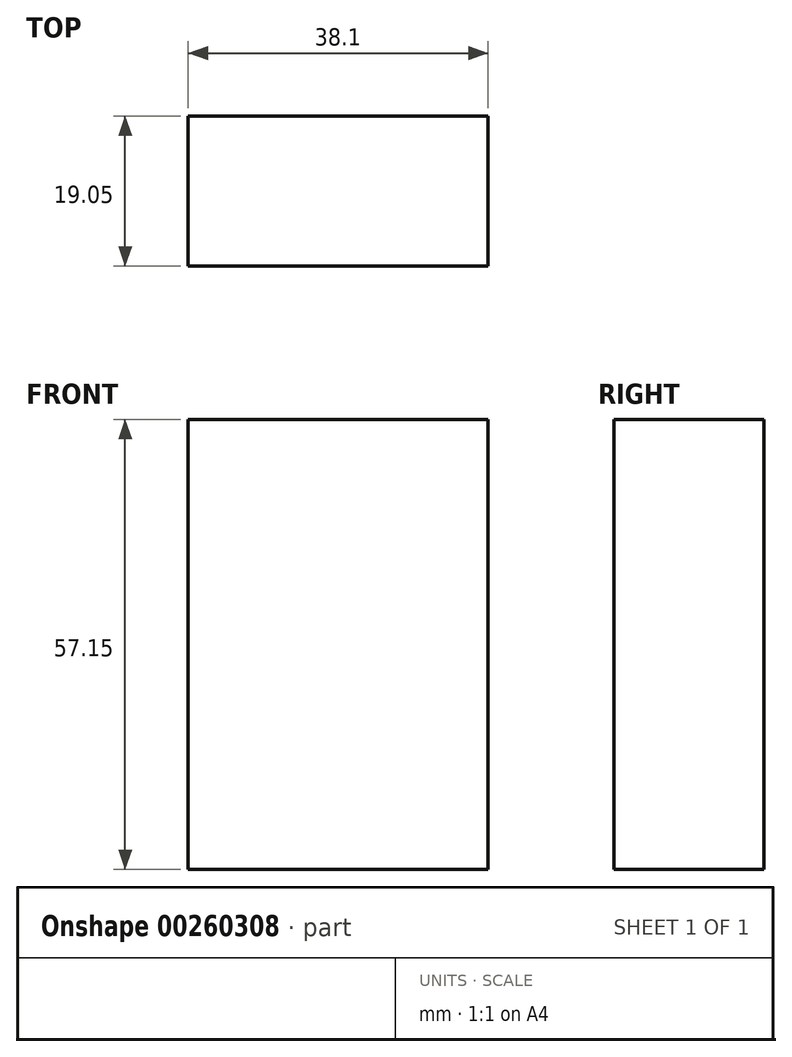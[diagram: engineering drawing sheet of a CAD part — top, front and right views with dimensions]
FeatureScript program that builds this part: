
annotation { "Feature Type Name" : "Feature", "Feature Type Description" : "" }
export const myFeature = defineFeature(function(context is Context, id is Id, definition is map)
    precondition{}
    {
        {
            var Q0;
            Q0=qCreatedBy(makeId("Front.planeOp"),FACE);
            var sketch = newSketch(context, id + "F0", { "sketchPlane" : qUnion([Q0])});
            skLineSegment(sketch, "E0.bottom", {"start": v(-54.15, 47.37) * mm, "end": v(-35.1, 47.37) * mm});
            skLineSegment(sketch, "E0.top", {"start": v(-54.15, 28.32) * mm, "end": v(-35.1, 28.32) * mm});
            skLineSegment(sketch, "E0.left", {"start": v(-54.15, 47.37) * mm, "end": v(-54.15, 28.32) * mm});
            skLineSegment(sketch, "E0.right", {"start": v(-35.1, 47.37) * mm, "end": v(-35.1, 28.32) * mm});
            skLineSegment(sketch, "E1.MirrorCS", {"start": v(-54.15, 9.27) * mm, "end": v(-54.15, 28.32) * mm});
            skLineSegment(sketch, "E2.MirrorCS", {"start": v(-35.1, 9.27) * mm, "end": v(-35.1, 28.32) * mm});
            skLineSegment(sketch, "E3.MirrorCS", {"start": v(-54.15, 9.27) * mm, "end": v(-35.1, 9.27) * mm});
            skLineSegment(sketch, "E4.MirrorCS", {"start": v(-54.15, 9.27) * mm, "end": v(-54.15, -9.78) * mm});
            skLineSegment(sketch, "E5.MirrorCS", {"start": v(-35.1, 9.27) * mm, "end": v(-35.1, -9.78) * mm});
            skLineSegment(sketch, "E6.MirrorCS", {"start": v(-54.15, -9.78) * mm, "end": v(-35.1, -9.78) * mm});
            skLineSegment(sketch, "E7.MirrorCS", {"start": v(-16.05, 47.37) * mm, "end": v(-35.1, 47.37) * mm});
            skLineSegment(sketch, "E8.MirrorCS", {"start": v(-16.05, 47.37) * mm, "end": v(-16.05, 28.32) * mm});
            skLineSegment(sketch, "E9.MirrorCS", {"start": v(-16.05, 28.32) * mm, "end": v(-35.1, 28.32) * mm});
            skLineSegment(sketch, "E10.MirrorCS", {"start": v(-16.05, 9.27) * mm, "end": v(-16.05, 28.32) * mm});
            skLineSegment(sketch, "E11.MirrorCS", {"start": v(-16.05, 9.27) * mm, "end": v(-35.1, 9.27) * mm});
            skLineSegment(sketch, "E12.MirrorCS", {"start": v(-16.05, 9.27) * mm, "end": v(-16.05, -9.78) * mm});
            skLineSegment(sketch, "E13.MirrorCS", {"start": v(-16.05, -9.78) * mm, "end": v(-35.1, -9.78) * mm});
            skSolve(sketch);
        }
        {
            var Q0;
            Q0=makeQuery(id+"F0.imprint","IMPRINT",FACE,{"disambiguationData":[TD([[makeQuery(id+"F0.imprint","IMPRINT",EDGE,{"derivedFrom":sQuery(id+"F0.wireOp",EDGE,"E3.MirrorCS")}),-1.0]])]});
            var Q1;
            Q1=makeQuery(id+"F0.imprint","IMPRINT",FACE,{"disambiguationData":[TD([[makeQuery(id+"F0.imprint","IMPRINT",EDGE,{"derivedFrom":sQuery(id+"F0.wireOp",EDGE,"E5.MirrorCS")}),1.0]])]});
            var Q2;
            Q2=makeQuery(id+"F0.imprint","IMPRINT",FACE,{"disambiguationData":[TD([[makeQuery(id+"F0.imprint","IMPRINT",EDGE,{"derivedFrom":sQuery(id+"F0.wireOp",EDGE,"E0.top")}),-1.0]])]});
            var Q3;
            Q3=makeQuery(id+"F0.imprint","IMPRINT",FACE,{"disambiguationData":[TD([[makeQuery(id+"F0.imprint","IMPRINT",EDGE,{"derivedFrom":sQuery(id+"F0.wireOp",EDGE,"E2.MirrorCS")}),-1.0]])]});
            var Q4;
            Q4=makeQuery(id+"F0.imprint","IMPRINT",FACE,{"disambiguationData":[TD([[makeQuery(id+"F0.imprint","IMPRINT",EDGE,{"derivedFrom":sQuery(id+"F0.wireOp",EDGE,"E0.bottom")}),-1.0]])]});
            var Q5;
            Q5=makeQuery(id+"F0.imprint","IMPRINT",FACE,{"disambiguationData":[TD([[makeQuery(id+"F0.imprint","IMPRINT",EDGE,{"derivedFrom":sQuery(id+"F0.wireOp",EDGE,"E7.MirrorCS")}),1.0]])]});
            extrude(context, id + "F1", {"entities" : qUnion([Q0, Q1, Q2, Q3, Q4, Q5]), "depth" : 19.05 * mm});
        }
    });
